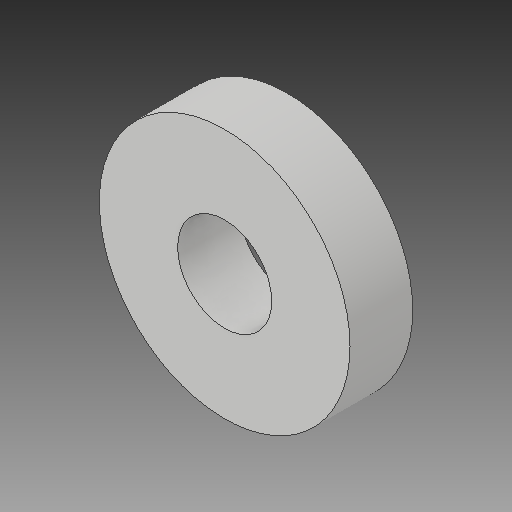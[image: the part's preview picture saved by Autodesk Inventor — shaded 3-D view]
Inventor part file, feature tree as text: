
AUTODESK INVENTOR PART (.ipt)
format: ipt  version: 2017 (Build 210142000, 142)  size: 95,232 bytes
history: native  units: in
note: dims shown in document units (in); Inventor stores cm internally (conversion verified against a paired STEP export)
features: extrude x1, sketch x1
ambient origin geometry x8: Origin, YZ Plane, XZ Plane, XY Plane, X Axis, Y Axis, Z Axis, Center Point
bodies: Solid1 (feature_tree)
feature tree (2):
  extrude  "Extrusion1"  Depth=0.125in
  sketch  "Sketch1"  dims[d0=0.5in d1=0.1875in d2=0.125in d3=0.0in]
